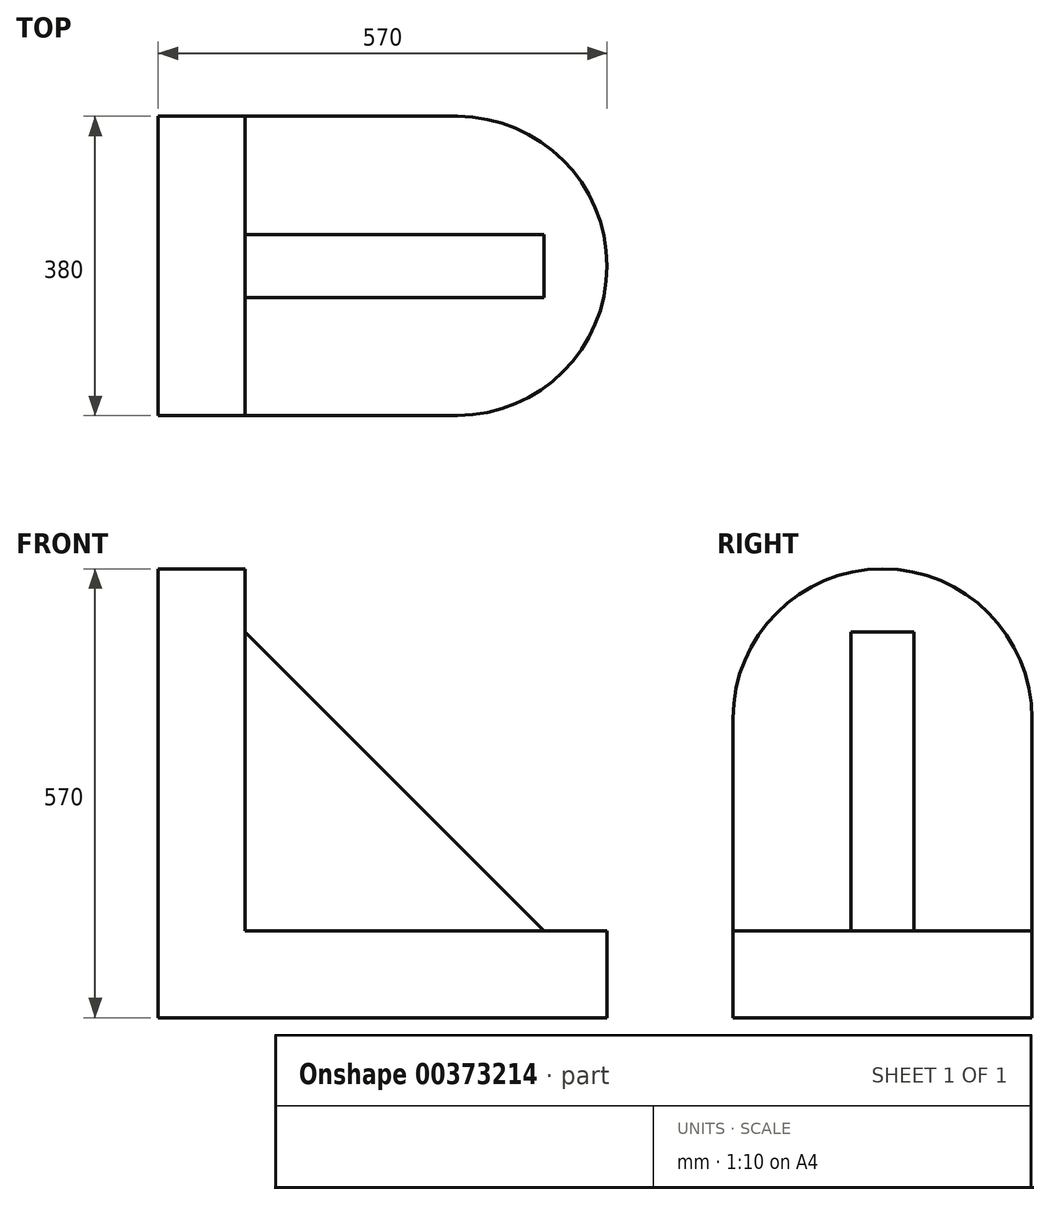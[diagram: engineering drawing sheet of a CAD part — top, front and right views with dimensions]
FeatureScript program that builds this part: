
annotation { "Feature Type Name" : "Feature", "Feature Type Description" : "" }
export const myFeature = defineFeature(function(context is Context, id is Id, definition is map)
    precondition{}
    {
        {
            var Q0;
            Q0=qCreatedBy(makeId("Top.planeOp"),FACE);
            var sketch = newSketch(context, id + "F0", { "sketchPlane" : qUnion([Q0])});
            skLineSegment(sketch, "E0.bottom", {"start": v(0, 0) * mm, "end": v(-380, 0) * mm});
            skLineSegment(sketch, "E0.top", {"start": v(0, 380) * mm, "end": v(-380, 380) * mm});
            skLineSegment(sketch, "E0.left", {"start": v(0, 0) * mm, "end": v(0, 380) * mm});
            skLineSegment(sketch, "E0.right", {"start": v(-380, 0) * mm, "end": v(-380, 380) * mm});
            skCircle(sketch, "E1", {"center": v(0, 190) * mm, "radius": 190 * mm});
            skSolve(sketch);
        }
        {
            var Q0;
            Q0 = qSketchRegion(id + "F0", true);
            extrude(context, id + "F1", {"entities" : qUnion([Q0]), "depth" : 110 * mm});
        }
        {
            var Q0;
            Q0=makeQuery(id+"F1.opExtrude","CAP_FACE",FACE,{"disambiguationData":[OSD([sQuery(id+"F0.wireOp",EDGE,"E0.bottom"),sQuery(id+"F0.wireOp",EDGE,"E0.top"),sQuery(id+"F0.wireOp",EDGE,"E0.right"),sQuery(id+"F0.wireOp",EDGE,"b5zdsOJD-4C38-NNnz-BdzW-2irRrQGt1rkH")])],"isStart":false});
            var sketch = newSketch(context, id + "F2", { "sketchPlane" : qUnion([Q0])});
            skLineSegment(sketch, "E2.bottom", {"start": v(-380, 380) * mm, "end": v(-270, 380) * mm});
            skLineSegment(sketch, "E2.top", {"start": v(-380, 0) * mm, "end": v(-270, 0) * mm});
            skLineSegment(sketch, "E2.left", {"start": v(-380, 380) * mm, "end": v(-380, 0) * mm});
            skLineSegment(sketch, "E2.right", {"start": v(-270, 380) * mm, "end": v(-270, 0) * mm});
            skSolve(sketch);
        }
        {
            var Q0;
            Q0=makeQuery(id+"F2.imprint","IMPRINT",FACE,{"disambiguationData":[TD([[makeQuery(id+"F2.imprint","IMPRINT",EDGE,{"derivedFrom":sQuery(id+"F2.wireOp",EDGE,"E2.bottom")}),1.0]])]});
            extrude(context, id + "F3", {"entities" : qUnion([Q0]), "operationType" : NewBodyOperationType.ADD, "depth" : 270 * mm});
        }
        {
            var Q0;
            Q0=makeQuery(id+"F3.boolean.opBoolean","MERGE",FACE,{"derivedFrom":[makeQuery(id+"F1.opExtrude","SWEPT_FACE",FACE,{"disambiguationData":[OSD([sQuery(id+"F0.wireOp",EDGE,"E0.bottom")])]}),makeQuery(id+"F3.opExtrude","SWEPT_FACE",FACE,{"disambiguationData":[OSD([sQuery(id+"F2.wireOp",EDGE,"E2.top")])]})]});
            var sketch = newSketch(context, id + "F4", { "sketchPlane" : qUnion([Q0])});
            skLineSegment(sketch, "E3", {"start": v(-270, 380) * mm, "end": v(0, 110) * mm});
            skSolve(sketch);
        }
        {
            var Q0;
            Q0=makeQuery(id+"F4.imprint","IMPRINT",FACE,{"disambiguationData":[TD([[makeQuery(id+"F4.imprint","IMPRINT",EDGE,{"derivedFrom":sQuery(id+"F4.wireOp",EDGE,"E3")}),-1.0]])]});
            extrude(context, id + "F5", {"entities" : qUnion([Q0]), "operationType" : NewBodyOperationType.REMOVE, "oppositeDirection" : true, "depth" : 150 * mm});
        }
        {
            var Q0;
            Q0=makeQuery(id+"FLaGTcrFp6KidVr_1.boolean.opBoolean","MERGE",FACE,{"derivedFrom":[makeQuery(id+"F3.boolean.opBoolean","MERGE",FACE,{"derivedFrom":[makeQuery(id+"F1.opExtrude","SWEPT_FACE",FACE,{"disambiguationData":[OSD([sQuery(id+"F0.wireOp",EDGE,"E0.top")])]}),makeQuery(id+"F3.opExtrude","SWEPT_FACE",FACE,{"disambiguationData":[OSD([sQuery(id+"F2.wireOp",EDGE,"E2.bottom")])]})]}),makeQuery(id+"FLaGTcrFp6KidVr_1.opExtrude","CAP_FACE",FACE,{"disambiguationData":[OSD([sQuery(id+"F0.wireOp",EDGE,"E0.bottom"),sQuery(id+"F2.wireOp",EDGE,"E2.top"),sQuery(id+"F2.wireOp",EDGE,"E2.right"),sQuery(id+"F4.wireOp",EDGE,"E3")])],"isStart":false})]});
            var sketch = newSketch(context, id + "F6", { "sketchPlane" : qUnion([Q0])});
            skLineSegment(sketch, "E4", {"start": v(270, 380) * mm, "end": v(270, 110) * mm});
            skLineSegment(sketch, "E5", {"start": v(270, 110) * mm, "end": v(0, 110) * mm});
            skLineSegment(sketch, "E6", {"start": v(0, 110) * mm, "end": v(270, 380) * mm});
            skSolve(sketch);
        }
        {
            var Q0;
            Q0=makeQuery(id+"F6.imprint","IMPRINT",FACE,{"disambiguationData":[TD([[makeQuery(id+"F6.imprint","IMPRINT",EDGE,{"derivedFrom":sQuery(id+"F6.wireOp",EDGE,"E4")}),-1.0]])]});
            extrude(context, id + "F7", {"entities" : qUnion([Q0]), "operationType" : NewBodyOperationType.REMOVE, "oppositeDirection" : true, "depth" : 150 * mm});
        }
        {
            var Q0;
            Q0=makeQuery(id+"F3.boolean.opBoolean","MERGE",FACE,{"derivedFrom":[makeQuery(id+"F1.opExtrude","SWEPT_FACE",FACE,{"disambiguationData":[OSD([sQuery(id+"F0.wireOp",EDGE,"E0.right")])]}),makeQuery(id+"F3.opExtrude","SWEPT_FACE",FACE,{"disambiguationData":[OSD([sQuery(id+"F2.wireOp",EDGE,"E2.left")])]})]});
            var sketch = newSketch(context, id + "F8", { "sketchPlane" : qUnion([Q0])});
            skCircle(sketch, "E7", {"center": v(-190, 380) * mm, "radius": 190 * mm});
            skSolve(sketch);
        }
        {
            var Q0;
            {var subQ1=sQuery(id+"F2.wireOp",EDGE,"E2.left");var subQ3=makeQuery(id+"F3.opExtrude","CAP_EDGE",EDGE,{"disambiguationData":[OSD([subQ1])],"isStart":false});Q0=makeQuery(id+"F8.imprint","IMPRINT",FACE,{"disambiguationData":[TD([[makeQuery(id+"F8.imprint","IMPRINT",EDGE,{"derivedFrom":subQ3}),-1.0]])]});}
            extrude(context, id + "F9", {"entities" : qUnion([Q0]), "operationType" : NewBodyOperationType.ADD, "oppositeDirection" : true, "depth" : 110 * mm});
        }
        {
            var Q0;
            Q0=makeQuery(id+"F9.boolean.opBoolean","MERGE",FACE,{"derivedFrom":[makeQuery(id+"F3.opExtrude","SWEPT_FACE",FACE,{"disambiguationData":[OSD([sQuery(id+"F2.wireOp",EDGE,"E2.right")])]}),makeQuery(id+"F9.opExtrude","CAP_FACE",FACE,{"disambiguationData":[OSD([sQuery(id+"F2.wireOp",EDGE,"E2.left"),sQuery(id+"F8.wireOp",EDGE,"E7")])],"isStart":false})]});
            var sketch = newSketch(context, id + "F10", { "sketchPlane" : qUnion([Q0])});
            skLineSegment(sketch, "E8", {"start": v(0, 110) * mm, "end": v(150, 110) * mm});
            skLineSegment(sketch, "E9", {"start": v(150, 110) * mm, "end": v(150, 490) * mm});
            skLineSegment(sketch, "E10", {"start": v(380, 110) * mm, "end": v(230, 110) * mm});
            skLineSegment(sketch, "E11", {"start": v(230, 110) * mm, "end": v(230, 490) * mm});
            skLineSegment(sketch, "E12", {"start": v(150, 490) * mm, "end": v(230, 490) * mm});
            skSolve(sketch);
        }
        {
            var Q0;
            Q0 = qSketchRegion(id + "F10", true);
            var Q1;
            {var subQ0=sQuery(id+"F10.wireOp",EDGE,"E9");Q1=makeQuery(id+"F10.imprint","IMPRINT",FACE,{"disambiguationData":[TD([[makeQuery(id+"F10.imprint","IMPRINT",EDGE,{"derivedFrom":subQ0}),-1.0]])]});}
            extrude(context, id + "F11", {"entities" : qUnion([Q0, Q1]), "operationType" : NewBodyOperationType.ADD, "depth" : 380 * mm});
        }
        {
            var Q0;
            Q0=makeQuery(id+"F11.opExtrude","SWEPT_FACE",FACE,{"disambiguationData":[OSD([sQuery(id+"F10.wireOp",EDGE,"E9")])]});
            var sketch = newSketch(context, id + "F12", { "sketchPlane" : qUnion([Q0])});
            skLineSegment(sketch, "E13", {"start": v(-270, 490) * mm, "end": v(110, 110) * mm});
            skSolve(sketch);
        }
        {
            var Q0;
            Q0=makeQuery(id+"F12.imprint","IMPRINT",FACE,{"disambiguationData":[TD([[makeQuery(id+"F12.imprint","IMPRINT",EDGE,{"derivedFrom":sQuery(id+"F12.wireOp",EDGE,"E13")}),1.0]])]});
            extrude(context, id + "F13", {"entities" : qUnion([Q0]), "operationType" : NewBodyOperationType.REMOVE, "oppositeDirection" : true, "depth" : 80 * mm});
        }
    });
